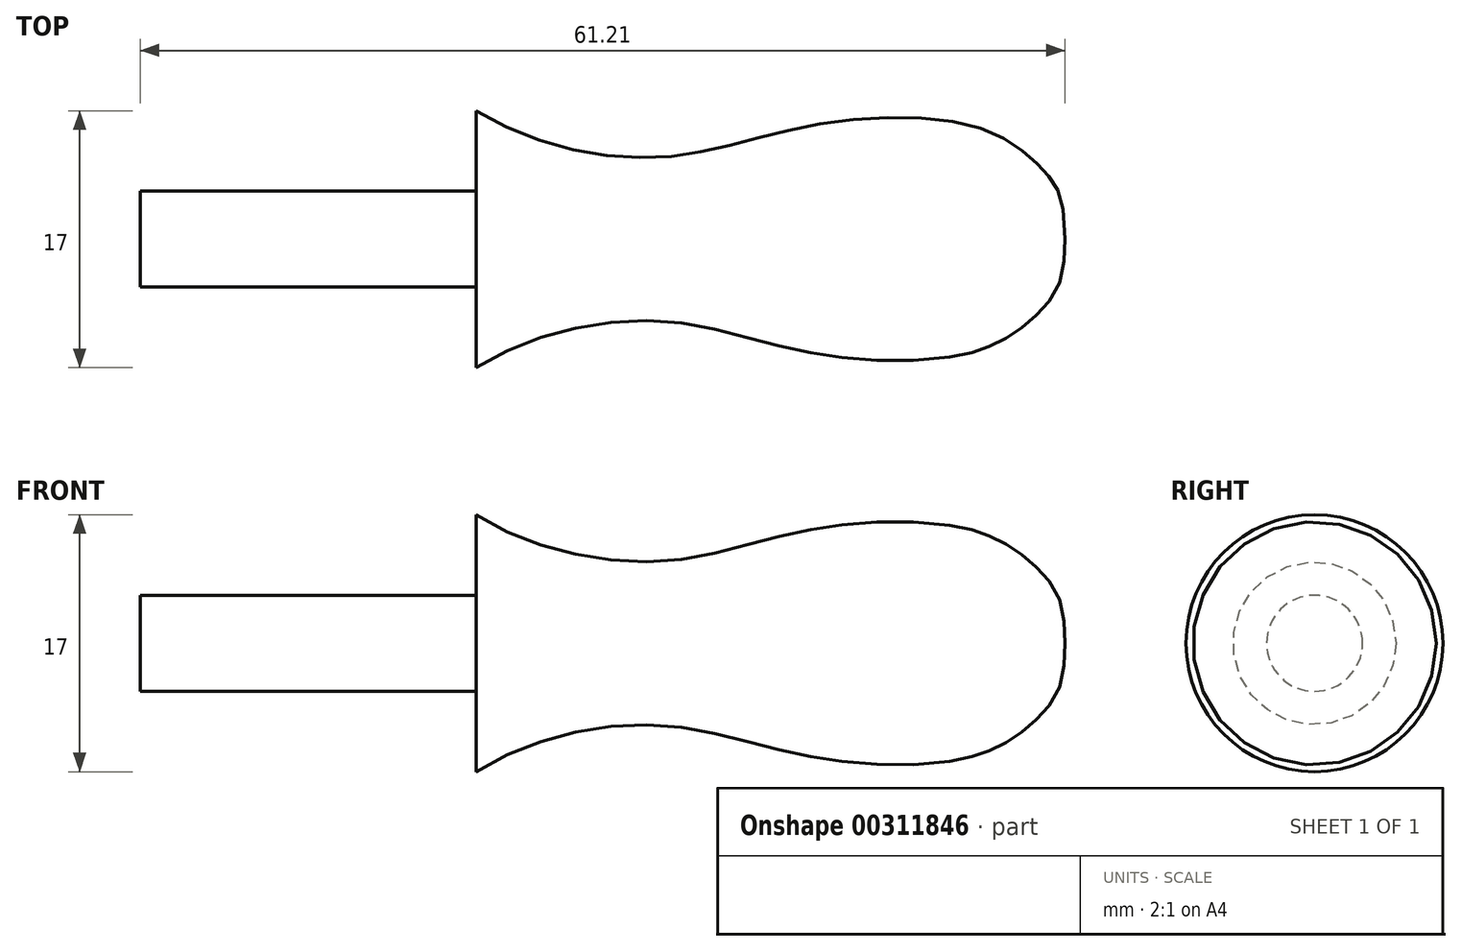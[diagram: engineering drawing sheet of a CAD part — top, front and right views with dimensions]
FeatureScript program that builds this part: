
annotation { "Feature Type Name" : "Feature", "Feature Type Description" : "" }
export const myFeature = defineFeature(function(context is Context, id is Id, definition is map)
    precondition{}
    {
        {
            var Q0;
            Q0=qCreatedBy(makeId("Top.planeOp"),FACE);
            var sketch = newSketch(context, id + "F0", { "sketchPlane" : qUnion([Q0])});
            skLineSegment(sketch, "E0", {"start": v(38.98, 0) * mm, "end": v(-22.23, 0) * mm});
            skLineSegment(sketch, "E1", {"start": v(-22.23, 0) * mm, "end": v(-22.23, 3.17) * mm});
            skLineSegment(sketch, "E2", {"start": v(-22.23, 3.17) * mm, "end": v(0, 3.17) * mm});
            skLineSegment(sketch, "E3", {"start": v(0, 3.17) * mm, "end": v(0, 8.5) * mm});
            skFitSpline(sketch, "E4", {"points": [v(0, 8.5) * mm, v(12.1, 5.42) * mm, v(21.93, 7.47) * mm, v(33.34, 7.34) * mm, v(37.57, 4.52) * mm, v(38.98, 0) * mm], "startDerivative": vector(44.73, -28.06) * mm, "endDerivative": vector(0, -55.64) * mm});
            skSolve(sketch);
        }
        {
            var Q0;
            Q0=makeQuery(id+"F0.imprint","IMPRINT",FACE,{"disambiguationData":[TD([[makeQuery(id+"F0.imprint","IMPRINT",EDGE,{"derivedFrom":sQuery(id+"F0.wireOp",EDGE,"E0")}),-1.0]])]});
            var Q1;
            Q1=sQuery(id+"F0.wireOp",EDGE,"E0");
            revolve(context, id + "F1", {"entities" : qUnion([Q0]), "axis" : qUnion([Q1]), "revolveType" : RevolveType.FULL});
        }
    });
